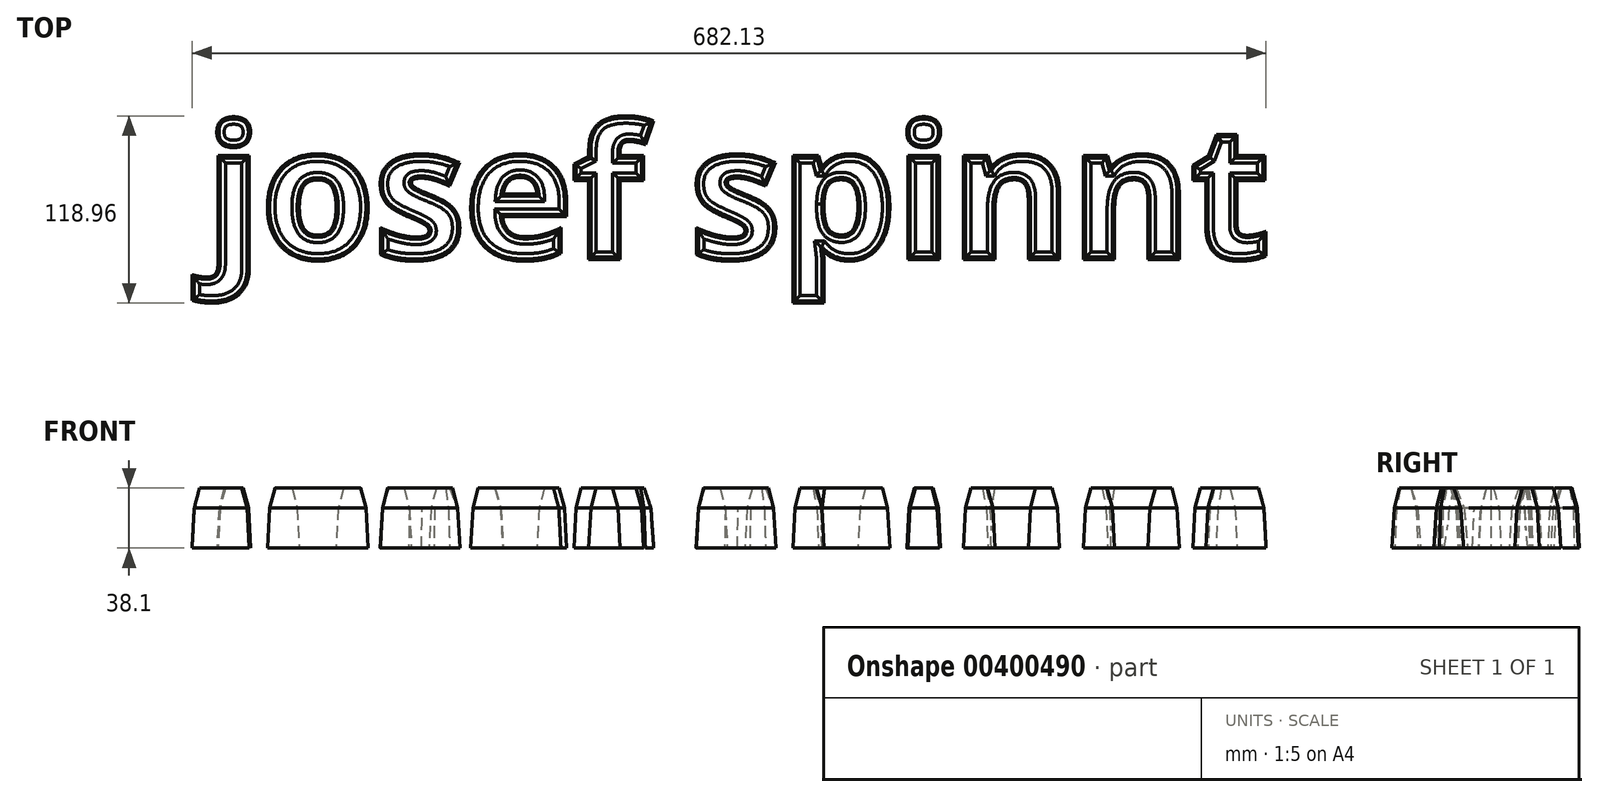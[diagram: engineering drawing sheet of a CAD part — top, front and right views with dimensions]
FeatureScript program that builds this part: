
annotation { "Feature Type Name" : "Feature", "Feature Type Description" : "" }
export const myFeature = defineFeature(function(context is Context, id is Id, definition is map)
    precondition{}
    {
        {
            var Q0;
            Q0=qCreatedBy(makeId("Top.planeOp"),FACE);
            var sketch = newSketch(context, id + "F0", { "sketchPlane" : qUnion([Q0])});
            skText(sketch, "E0", { "text": "josef spinnt", "fontName": "OpenSans-Bold.ttf"});
            const initialGuessF0  = {"E0": [-0.11026, -0.05485, 1, 0, 0.08328]};
            skSetInitialGuess(sketch, initialGuessF0);
            skSolve(sketch);
        }
        {
            var Q0;
            Q0 = qSketchRegion(id + "F0", true);
            extrude(context, id + "F1", {"entities" : qUnion([Q0]), "depth" : 12.7 * mm, "hasDraft" : true, "draftAngle" : 15 * degree, "draftPullDirection" : true, "hasSecondDirection" : true, "secondDirectionOppositeDirection" : true, "secondDirectionDepth" : 25.4 * mm, "hasSecondDirectionDraft" : true, "secondDirectionDraftAngle" : 3 * degree});
        }
    });
